FCSTD DOCUMENT  (FreeCAD 0.21R33771 (Git))
Label: longbone
License: All rights reserved
LicenseURL: http://en.wikipedia.org/wiki/All_rights_reserved
objects: Sketcher::SketchObject×1
note: 1 computed .brp shape members not serialized (recipe doc carries the construction recipe); baked Part::Feature solids carry a one-line shape summary decoded from their .brp

FEATURE [Sketcher::SketchObject] Sketch
  FullyConstrained = true
  sketch-geometry (84):
    g0-g18: Circle x19 (B-spline internal-alignment scaffolding for g19; pole/knot coordinates omitted)
    g19: BSplineCurve PolesCount=19 KnotsCount=17 Degree=3 IsPeriodic=0
    g20-g35: GeomPoint x16 (B-spline internal-alignment scaffolding for g19; pole/knot coordinates omitted)
    g36: GeomPoint X=-2 Y=-1.1 Z=0
    g37: LineSegment StartX=-2 StartY=0.55 StartZ=0 EndX=0 EndY=0.856758 EndZ=0
    g38: GeomPoint X=0 Y=-1.71993 Z=0
    g39: Circle CenterX=-1.23048 CenterY=-1.88478 CenterZ=0 NormalX=0 NormalY=0 NormalZ=1 AngleXU=0 Radius=1
    g40: Circle CenterX=0 CenterY=-1.55508 CenterZ=0 NormalX=0 NormalY=0 NormalZ=1 AngleXU=0 Radius=1
    g41: Circle CenterX=1.23048 CenterY=-1.88478 CenterZ=0 NormalX=0 NormalY=0 NormalZ=1 AngleXU=0 Radius=1
    g42: BSplineCurve PolesCount=3 KnotsCount=2 Degree=2 IsPeriodic=0
    g43: GeomPoint X=-1.23048 Y=-1.88478 Z=0
    g44: GeomPoint X=1.23048 Y=-1.88478 Z=0
    g45: Circle CenterX=-0.75 CenterY=0.0291062 CenterZ=0 NormalX=0 NormalY=0 NormalZ=1 AngleXU=0 Radius=1
    g46: Circle CenterX=0 CenterY=0.230068 CenterZ=0 NormalX=0 NormalY=0 NormalZ=1 AngleXU=0 Radius=1
    g47: Circle CenterX=0.75 CenterY=0.0291062 CenterZ=0 NormalX=0 NormalY=0 NormalZ=1 AngleXU=0 Radius=1
    g48: BSplineCurve PolesCount=3 KnotsCount=2 Degree=2 IsPeriodic=0
    g49: GeomPoint X=-0.75 Y=0.0291062 Z=0
    g50: GeomPoint X=0.75 Y=0.0291062 Z=0
    g51: LineSegment StartX=-1.23048 StartY=-1.88478 StartZ=0 EndX=0 EndY=-1.55508 EndZ=0
    g52: LineSegment StartX=-1.23048 StartY=-1.88478 StartZ=0 EndX=0 EndY=-1.88478 EndZ=0
    g53: LineSegment StartX=-1.23048 StartY=-1.88478 StartZ=0 EndX=-0.615239 EndY=-1.76115 EndZ=0
    g54-g57: Circle x4 (B-spline internal-alignment scaffolding for g58; pole/knot coordinates omitted)
    g58: BSplineCurve PolesCount=4 KnotsCount=2 Degree=3 IsPeriodic=0
    g59: GeomPoint X=-0.75 Y=0.0291062 Z=0
    g60: GeomPoint X=-0.615239 Y=-1.76115 Z=0
    g61: GeomPoint X=-0.615239 Y=-1.88478 Z=0
    g62-g65: Circle x4 (B-spline internal-alignment scaffolding for g66; pole/knot coordinates omitted)
    g66: BSplineCurve PolesCount=4 KnotsCount=2 Degree=3 IsPeriodic=0
    g67: GeomPoint X=0.75 Y=0.0291062 Z=0
    g68: GeomPoint X=0.615239 Y=-1.76115 Z=0
    g69: GeomPoint X=-0.68262 Y=-0.866019 Z=0
    g70: LineSegment StartX=-0.75 StartY=0.0291062 StartZ=0 EndX=-1.35245 EndY=0.631553 EndZ=0
    g71: LineSegment StartX=0.75 StartY=0.0291062 StartZ=0 EndX=1.35245 EndY=0.631553 EndZ=0
    g72: LineSegment StartX=-1.1 StartY=-5.96993 StartZ=0 EndX=1.1 EndY=-5.96993 EndZ=0
    g73: LineSegment StartX=-2 StartY=0.55 StartZ=0 EndX=0 EndY=0.55 EndZ=0
    g74: LineSegment StartX=-0.615239 StartY=-1.76115 StartZ=0 EndX=-0.615239 EndY=-0.866019 EndZ=0
    g75: LineSegment StartX=-0.75 StartY=-0.866019 StartZ=0 EndX=-0.75 EndY=0.0291062 EndZ=0
    g76: GeomPoint X=-0.5 Y=0.780068 Z=0
    g77: GeomPoint X=-0.75 Y=0.741723 Z=0
    g78: GeomPoint X=-1 Y=0.153379 Z=0
    g79: LineSegment StartX=-1.41314e-10 StartY=0.780068 StartZ=0 EndX=0 EndY=0.230068 EndZ=0
    g80: GeomPoint X=-2 Y=-0.275 Z=0
    g81: LineSegment StartX=-2 StartY=0 StartZ=0 EndX=-2 EndY=0.55 EndZ=0
    g82: GeomPoint X=-2 Y=-1.65 Z=0
    g83: LineSegment StartX=-0.75 StartY=0.0291062 StartZ=0 EndX=0 EndY=0.230068 EndZ=0
  constraints (138):
    c: Weight(g0) = 1
    c: Equal(g0,g2)
    c: Equal(g0,g4)
    c: Equal(g0,g6)
    c: Equal(g0,g8)
    c: Equal(g0,g10)
    c: Equal(g0,g12)
    c: Equal(g0,g14)
    c: Equal(g0,g16)
    c: Equal(g0,g18)
    c: InternalAlignment(g0-g18 -> g19) x19
    c: InternalAlignment(g20-g35 -> g19) x16
    c: Coincident(g2,g21)
    c: Coincident(g4,g23)
    c: Coincident(g6,g25)
    c: Coincident(g8,g27)
    c: Coincident(g10,g29)
    c: Coincident(g12,g31)
    c: Coincident(g14,g33)
    c: Coincident(g16,g34)
    c: Weight(g9) = 0.5
    c: Equal(g7,g11)
    c: Weight(g7) = 0.5
    c: Equal(g5,g13)
    c: Weight(g5) = 0.5
    c: Equal(g3,g15)
    c: Weight(g3) = 0.5
    c: Equal(g1,g17)
    c: Weight(g1) = 0.5
    c: Vertical(g19,g17)
    c: Vertical(g17,g15)
    c: Vertical(g11,g13)
    c: PointOnObject(g9,g-2)
    c: Symmetric(g7,g11,g-2)
    c: Horizontal(g5,g13)
    c: DistanceY(g5,g7) = 1.1  'radius_y'
    c: DistanceX(g7,g9) = 2  'radius_x'
    c: Horizontal(g2,g16)
    c: PointOnObject(g6,g-1)
    c: DistanceX(g3,g15) = 2.2  'bone_width'
    c: Symmetric(g19,g19,g-2)
    c: Vertical(g7,g5)
    c: Symmetric(g6,g36,g5)
    c: Coincident(g37,g7)
    c: Coincident(g37,g9)
    c: PointOnObject(g38,g-2)
    c: Weight(g39) = 1
    c: Equal(g39,g40)
    c: PointOnObject(g40,g-2)
    c: Equal(g39,g41)
    c: InternalAlignment(g39,g42)
    c: InternalAlignment(g40,g42)
    c: InternalAlignment(g41,g42)
    c: InternalAlignment(g43,g42)
    c: InternalAlignment(g44,g42)
    c: Symmetric(g42,g42,g-2)
    c: PointOnObject(g38,g42)
    c: PointOnObject(g53,g42)
    c: Symmetric(g2,g19,g1)
    c: Vertical(g3,g19)
    c: Horizontal(g3,g15)
    c: Weight(g45) = 1
    c: Equal(g45,g46)
    c: Equal(g45,g47)
    c: InternalAlignment(g45,g48)
    c: InternalAlignment(g46,g48)
    c: InternalAlignment(g47,g48)
    c: InternalAlignment(g49,g48)
    c: InternalAlignment(g50,g48)
    c: Symmetric(g48,g48,g-2)
    c: Coincident(g51,g40)
    c: PointOnObject(g52,g-2)
    c: Horizontal(g52)
    c: Angle(g52,g51) = 0.261799  'curve_angle'
    c: Weight(g54) = 1
    c: Coincident(g58,g48)
    c: Equal(g54,g55)
    c: Equal(g54,g56)
    c: Equal(g54,g57)
    c: InternalAlignment(g54-g57 -> g58) x4
    c: InternalAlignment(g59,g58)
    c: InternalAlignment(g60,g58)
    c: Symmetric(g52,g52,g61)
    c: Vertical(g53,g61)
    c: Weight(g62) = 1
    c: Coincident(g66,g48)
    c: Equal(g62,g63)
    c: Equal(g62,g64)
    c: Equal(g62,g65)
    c: InternalAlignment(g62-g65 -> g66) x4
    c: InternalAlignment(g67,g66)
    c: InternalAlignment(g68,g66)
    c: Symmetric(g63,g55,g-2)
    c: Symmetric(g64,g56,g-2)
    c: Symmetric(g48,g53,g69)
    c: Coincident(g51,g53)
    c: Coincident(g51,g52)
    c: Coincident(g39,g51)
    c: PointOnObject(g39,g19)
    c: Symmetric(g58,g66,g-2)
    c: Vertical(g58,g56)
    c: Coincident(g58,g53)
    c: Coincident(g70,g48)
    c: Coincident(g71,g48)
    c: Symmetric(g70,g71,g-2)
    c: Coincident(g72,g19)
    c: Coincident(g72,g19)
    c: PointOnObject(g46,g-2)
    c: DistanceY(g38,g28) = 2.5  'cart_thick'
    c: Coincident(g73,g7)
    c: Horizontal(g73)
    c: PointOnObject(g73,g-2)
    c: Angle(g73,g37) = 0.152193  'head_angle'
    c: DistanceY(g19,g38) = 4.25  'head_height'
    c: Vertical(g55,g48)
    c: Horizontal(g55,g56)
    c: Coincident(g74,g58)
    c: Coincident(g74,g56)
    c: Coincident(g75,g55)
    c: Coincident(g75,g48)
    c: Equal(g74,g75)
    c: Symmetric(g8,g9,g76)
    c: Symmetric(g8,g76,g77)
    c: Vertical(g48,g77)
    c: Symmetric(g5,g9,g78)
    c: Coincident(g79,g28)
    c: Coincident(g79,g46)
    c: Symmetric(g6,g5,g80)
    c: Angle(g70,g73) = 0.785398
    c: PointOnObject(g70,g19)
    c: Coincident(g81,g6)
    c: Coincident(g81,g7)
    c: Equal(g81,g79)
    c: Symmetric(g82,g5,g36)
    c: Horizontal(g82,g3)
    c: Coincident(g83,g48)
    c: Coincident(g83,g46)
    c: Angle(g83,g70) = 2.0944
